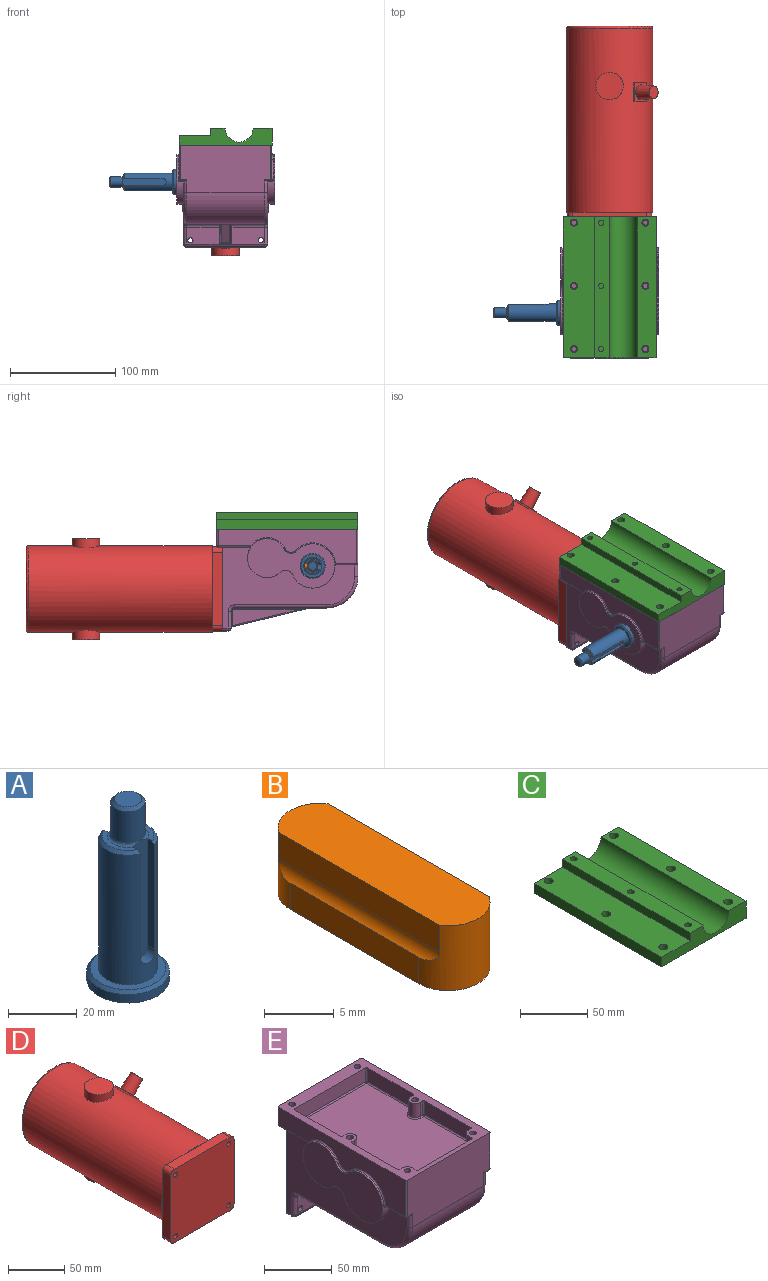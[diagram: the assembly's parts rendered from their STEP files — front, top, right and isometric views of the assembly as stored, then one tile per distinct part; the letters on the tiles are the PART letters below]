
ASSEMBLY  parts=5 mates=3
PART A: 21 faces, bbox 24x24x64 mm
  f0: plane 13.75x4.5mm, normal (0,0,1), area 22.7mm2, adj f4,f14,f17,f20
  f1: plane 13.75x4.5mm, normal (0,0,1), area 22.7mm2, adj f3,f12,f16,f20
  f2: cylinder r=8.5mm len=46mm, axis (0,0,1), area 1974.2mm2, adj f3,f4,f7,f12,f13,f14,f16,f17
  f3: cone r=7.5mm half-angle=45deg, axis (0,0,-1), area 26.8mm2, adj f1,f2,f12,f16
  f4: cone r=7.5mm half-angle=45deg, axis (0,0,-1), area 26.8mm2, adj f0,f2,f14,f17
  f5: plane 24x24mm, normal (0,0,-1), area 452.4mm2, adj f6
  f6: cylinder r=12mm len=24mm, axis (0,0,1), area 226.2mm2, adj f5,f10
  f7: plane 22x22mm, normal (0,0,1), area 153.2mm2, adj f2,f10
  f8: cylinder r=4.98mm len=11mm, axis (0,0,1), area 344.2mm2, adj f11,f20
  f9: plane 7.96x7.96mm, normal (0,0,1), area 49.8mm2, adj f11
  f10: cone r=11mm half-angle=45deg, axis (0,0,-1), area 102.2mm2, adj f6,f7
  f11: cone r=3.98mm half-angle=45deg, axis (0,0,-1), area 39.8mm2, adj f8,f9
  f12: plane 38.04x2.98mm, normal (1,0,0), area 111.7mm2, adj f1,f2,f3,f13,f15,f20
  f13: cylinder r=3mm len=6mm, axis (0,-1,0), area 30.4mm2, adj f2,f12,f14,f15
  f14: plane 38.04x2.98mm, normal (-1,0,0), area 111.7mm2, adj f0,f2,f4,f13,f15,f20
  f15: plane 41.8x6mm, normal (0,1,0), area 244.4mm2, adj f12,f13,f14,f20
  f16: plane 38.04x2.98mm, normal (1,0,0), area 111.7mm2, adj f1,f2,f3,f18,f19,f20
  f17: plane 38.04x2.98mm, normal (-1,0,0), area 111.7mm2, adj f0,f2,f4,f18,f19,f20
  f18: cylinder r=3mm len=6mm, axis (0,1,0), area 30.4mm2, adj f2,f16,f17,f19
  f19: plane 41.8x6mm, normal (0,-1,0), area 244.4mm2, adj f16,f17,f18,f20
  f20: torus R=5.98mm, axis (0,0,1), area 42.4mm2, adj f0,f1,f8,f12,f14,f15,f16,f17
PART B: 10 faces, bbox 6x19.1x5.7 mm
  f0: cylinder r=3mm len=6mm, axis (0,0,-1), area 42.5mm2, adj f1,f3,f4,f5,f6,f7,f8,f9
  f1: plane 13.05x2.32mm, normal (1,0,0), area 30.2mm2, adj f0,f2,f5,f8
  f2: cylinder r=3mm len=6mm, axis (0,0,-1), area 42.5mm2, adj f1,f3,f4,f5,f6,f7,f8,f9
  f3: plane 19.05x5mm, normal (0,0,1), area 91.3mm2, adj f0,f2,f7,f9
  f4: plane 13.05x2.32mm, normal (-1,0,0), area 30.2mm2, adj f0,f2,f5,f6
  f5: plane 19.05x6mm, normal (0,0,-1), area 106.6mm2, adj f0,f1,f2,f4
  f6: cylinder r=1.27mm len=16.37mm, axis (0,-1,0), area 18.3mm2, adj f0,f2,f4,f7
  f7: plane 16.37x2.37mm, normal (-1,0,0), area 38.9mm2, adj f0,f2,f3,f6
  f8: cylinder r=1.27mm len=16.37mm, axis (0,-1,0), area 18.3mm2, adj f0,f1,f2,f9
  f9: plane 16.37x2.37mm, normal (1,0,0), area 38.9mm2, adj f0,f2,f3,f8
PART C: 22 faces, bbox 88.3x134x15.9 mm
  f0: plane 134x15.88mm, normal (1,0,0), area 2127.2mm2, adj f1,f7,f8,f9
  f1: plane 134x88.25mm, normal (0,0,-1), area 11614mm2, adj f0,f2,f8,f9,f16,f17,f18,f19
  f2: plane 134x8.8mm, normal (-1,0,0), area 1179.2mm2, adj f1,f3,f8,f9
  f3: plane 134x29.8mm, normal (0,0,1), area 3887.4mm2, adj f2,f4,f8,f9,f19,f20,f21
  f4: plane 134x7.08mm, normal (-1,0,0), area 948mm2, adj f3,f5,f8,f9
  f5: plane 134x13.75mm, normal (0,0,1), area 1783.6mm2, adj f4,f6,f8,f9,f10,f12,f14
  f6: cylinder r=13.36mm len=134mm, axis (0,1,0), area 5520.3mm2, adj f5,f7,f8,f9
  f7: plane 134x18mm, normal (0,0,1), area 2306.2mm2, adj f0,f6,f8,f9,f16,f17,f18
  f8: plane 88.25x15.88mm, normal (0,-1,0), area 920.1mm2, adj f0,f1,f2,f3,f4,f5,f6,f7
  f9: plane 88.25x15.88mm, normal (0,1,0), area 920.1mm2, adj f0,f1,f2,f3,f4,f5,f6,f7
  f10: cylinder r=2.5mm len=7.08mm, axis (0,0,-1), area 111.1mm2, adj f5,f11
  f11: plane 5x5mm, normal (0,0,1), area 19.6mm2, adj f10
  f12: cylinder r=2.5mm len=7.08mm, axis (0,0,-1), area 111.1mm2, adj f5,f13
  f13: plane 5x5mm, normal (0,0,1), area 19.6mm2, adj f12
  f14: cylinder r=2.5mm len=7.08mm, axis (0,0,-1), area 111.1mm2, adj f5,f15
  f15: plane 5x5mm, normal (0,0,1), area 19.6mm2, adj f14
  f16: cylinder r=3.35mm len=15.88mm, axis (0,0,1), area 334.1mm2, adj f1,f7
  f17: cylinder r=3.35mm len=15.88mm, axis (0,0,1), area 334.1mm2, adj f1,f7
  f18: cylinder r=3.35mm len=15.88mm, axis (0,0,1), area 334.1mm2, adj f1,f7
  f19: cylinder r=3.35mm len=8.8mm, axis (0,0,1), area 185.2mm2, adj f1,f3
  f20: cylinder r=3.35mm len=8.8mm, axis (0,0,1), area 185.2mm2, adj f1,f3
  f21: cylinder r=3.35mm len=8.8mm, axis (0,0,1), area 185.2mm2, adj f1,f3
PART D: 35 faces, bbox 90.4x187x96 mm
  f0: cylinder r=41mm len=175mm, axis (0,-1,0), area 43714.5mm2, adj f1,f2,f3,f12,f14,f15,f16,f18
  f1: plane 31x31mm, normal (0,1,0), area 266.8mm2, adj f0,f4,f7,f11,f33
  f2: plane 31x31mm, normal (0,1,0), area 266.8mm2, adj f0,f6,f8,f11,f32
  f3: plane 31x31mm, normal (0,1,0), area 266.8mm2, adj f0,f5,f6,f9,f31
  f4: plane 70x10mm, normal (1,0,0), area 700mm2, adj f1,f12,f13,f16,f30,f33
  f5: plane 70x10mm, normal (0,0,-1), area 700mm2, adj f3,f12,f13,f18,f30,f31
  f6: plane 70x10mm, normal (-1,0,0), area 700mm2, adj f2,f3,f13,f15,f31,f32
  f7: cylinder r=2.5mm len=10mm, axis (0,-1,0), area 157.1mm2, adj f1,f13
  f8: cylinder r=2.5mm len=10mm, axis (0,-1,0), area 157.1mm2, adj f2,f13
  f9: cylinder r=2.5mm len=10mm, axis (0,-1,0), area 157.1mm2, adj f3,f13
  f10: cylinder r=2.5mm len=10mm, axis (0,-1,0), area 157.1mm2, adj f12,f13
  f11: plane 70x10mm, normal (0,0,1), area 700mm2, adj f1,f2,f13,f14,f32,f33
  f12: plane 31x31mm, normal (0,1,0), area 266.8mm2, adj f0,f4,f5,f10,f30
  f13: plane 80x80mm, normal (0,-1,0), area 6300mm2, adj f4,f5,f6,f7,f8,f9,f10,f11
  f14: plane 18x1mm, normal (0,-1,0), area 12mm2, adj f0,f11
  f15: plane 18x1mm, normal (0,-1,0), area 12mm2, adj f0,f6
  f16: plane 18x1mm, normal (0,-1,0), area 12mm2, adj f0,f4
  f17: plane 78x78mm, normal (0,1,0), area 4778.4mm2, adj f34
  f18: plane 18x1mm, normal (0,-1,0), area 12mm2, adj f0,f5
  f19: plane 26x26mm, normal (0,0,1), area 530.9mm2, adj f20
  f20: cylinder r=13mm len=26mm, axis (0,0,-1), area 657.6mm2, adj f0,f19
  f21: cylinder r=13mm len=26mm, axis (0,0,-1), area 657.6mm2, adj f0,f22
  f22: plane 26x26mm, normal (0,0,-1), area 530.9mm2, adj f21
  f23: plane 18x1.26mm, normal (-0.71,0,0.71), area 32.2mm2, adj f0,f25,f26,f27
  f24: plane 18x1.26mm, normal (0.71,0,-0.71), area 32.2mm2, adj f0,f25,f26,f27
  f25: plane 12.58x12.58mm, normal (0,1,0), area 20.2mm2, adj f0,f23,f24,f27
  f26: plane 12.58x12.58mm, normal (0,-1,0), area 20.2mm2, adj f0,f23,f24,f27
  f27: plane 18x11.31mm, normal (0.71,0,0.71), area 134.1mm2, adj f23,f24,f25,f26,f28
  f28: cone r=7mm half-angle=3deg, axis (-0.71,0,-0.71), area 701.1mm2, adj f27,f29
  f29: plane 12.22x8.64mm, normal (0.71,0,0.71), area 117.2mm2, adj f28
  f30: cylinder r=5mm len=10mm, axis (0,-1,0), area 78.5mm2, adj f4,f5,f12,f13
  f31: cylinder r=5mm len=10mm, axis (0,1,0), area 78.5mm2, adj f3,f5,f6,f13
  f32: cylinder r=5mm len=10mm, axis (0,-1,0), area 78.5mm2, adj f2,f6,f11,f13
  f33: cylinder r=5mm len=10mm, axis (0,1,0), area 78.5mm2, adj f1,f4,f11,f13
  f34: torus R=39mm, axis (0,1,0), area 795mm2, adj f0,f17
PART E: 163 faces, bbox 93x136.5x97 mm
  f0: cylinder r=3mm len=31mm, axis (1,0,0), area 146.1mm2, adj f3,f10,f45,f150
  f1: plane 134x88mm, normal (0,0,1), area 2921.3mm2, adj f2,f24,f25,f26,f48,f57,f64,f69
  f2: plane 86x45mm, normal (0,-1,0), area 3726mm2, adj f1,f31,f32,f34,f48,f49,f56,f57
  f3: plane 87.5x74mm, normal (0,0,-1), area 5616.9mm2, adj f0,f31,f35,f41,f42,f149,f151,f154
  f4: plane 80x80mm, normal (0,1,0), area 6317.6mm2, adj f5,f6,f7,f8,f9,f11,f13,f23
  f5: plane 125.5x77mm, normal (1,0,0), area 4068.3mm2, adj f4,f19,f20,f21,f22,f23,f32,f33
  f6: plane 125.5x77mm, normal (-1,0,0), area 4068.3mm2, adj f4,f15,f16,f17,f18,f23,f34,f38
  f7: plane 74x5mm, normal (0,0,-1), area 370mm2, adj f4,f37,f43,f44
  f8: cylinder r=2.5mm len=8mm, axis (0,1,0), area 125.7mm2, adj f4,f10
  f9: cylinder r=2.5mm len=8mm, axis (0,1,0), area 125.7mm2, adj f4,f10
  f10: plane 74x16mm, normal (0,-1,0), area 957mm2, adj f0,f8,f9,f36,f42,f43,f47,f152
  f11: cylinder r=2.5mm len=6mm, axis (0,1,0), area 94.2mm2, adj f4,f12
  f12: plane 5x5mm, normal (0,1,0), area 19.6mm2, adj f11
  f13: cylinder r=2.5mm len=6mm, axis (0,1,0), area 94.2mm2, adj f4,f14
  f14: plane 5x5mm, normal (0,1,0), area 19.6mm2, adj f13
  f15: plane 20x3.76mm, normal (0,0,-1), area 60.5mm2, adj f6,f34,f49,f51,f52
  f16: cylinder r=21mm len=42mm, axis (-1,0,0), area 449.8mm2, adj f6,f17,f27,f28,f52,f53,f54
  f17: cylinder r=7.11mm len=11.42mm, axis (-1,0,0), area 88.9mm2, adj f6,f16,f18,f27
  f18: cylinder r=18.5mm len=37mm, axis (-1,0,0), area 402.3mm2, adj f6,f17,f27,f28,f58,f59,f61
  f19: plane 20x3.76mm, normal (0,0,-1), area 60.5mm2, adj f5,f32,f56,f62,f63
  f20: cylinder r=21mm len=42mm, axis (-1,0,0), area 449.8mm2, adj f5,f21,f29,f30,f62,f66,f68
  f21: cylinder r=7.11mm len=11.42mm, axis (-1,0,0), area 88.9mm2, adj f5,f20,f22,f30
  f22: cylinder r=18.5mm len=37mm, axis (-1,0,0), area 402.3mm2, adj f5,f21,f29,f30,f73,f75,f76
  f23: plane 86x29.51mm, normal (0,0,-1), area 537.1mm2, adj f4,f5,f6,f59,f65,f70,f74,f76
  f24: plane 86x16mm, normal (0,1,0), area 1376mm2, adj f1,f64,f69,f70
  f25: plane 132x33mm, normal (1,0,0), area 2354mm2, adj f1,f57,f63,f68,f69,f71,f73,f74
  f26: plane 132x33mm, normal (-1,0,0), area 2354mm2, adj f1,f48,f51,f54,f55,f58,f64,f65
  f27: plane 82.96x47mm, normal (-1,0,0), area 2565.2mm2, adj f16,f17,f18,f28
  f28: cylinder r=7.11mm len=11.55mm, axis (-1,0,0), area 20.5mm2, adj f16,f18,f27,f55
  f29: cylinder r=7.11mm len=11.55mm, axis (-1,0,0), area 20.5mm2, adj f20,f22,f30,f71
  f30: plane 82.96x47mm, normal (1,0,0), area 2565.2mm2, adj f20,f21,f22,f29
  f31: cylinder r=30mm len=74mm, axis (1,0,0), area 3487.2mm2, adj f2,f3,f33,f38
  f32: cylinder r=3mm len=12mm, axis (0,0,1), area 53.1mm2, adj f2,f5,f19,f33,f56
  f33: torus R=27mm, axis (1,0,0), area 214mm2, adj f5,f31,f32,f35
  f34: cylinder r=3mm len=12mm, axis (0,0,-1), area 53.1mm2, adj f2,f6,f15,f38,f49
  f35: cylinder r=3mm len=87.5mm, axis (0,-1,0), area 412.3mm2, adj f3,f5,f33,f39
  f36: cylinder r=3mm len=16mm, axis (0,0,-1), area 75.4mm2, adj f5,f10,f39,f40
  f37: cylinder r=3mm len=5mm, axis (0,-1,0), area 23.6mm2, adj f4,f5,f7,f40
  f38: torus R=27mm, axis (1,0,0), area 214mm2, adj f6,f31,f34,f41
  f39: torus R=6mm, axis (1,0,0), area 30.3mm2, adj f5,f35,f36,f42
  f40: sphere r=3mm, area 14.1mm2, adj f36,f37,f43
  f41: cylinder r=3mm len=87.5mm, axis (0,1,0), area 412.3mm2, adj f3,f6,f38,f45
  f42: cylinder r=3mm len=31mm, axis (1,0,0), area 146.1mm2, adj f3,f10,f39,f160
  f43: cylinder r=3mm len=74mm, axis (-1,0,0), area 348.7mm2, adj f7,f10,f40,f46
  f44: cylinder r=3mm len=5mm, axis (0,1,0), area 23.6mm2, adj f4,f6,f7,f46
  f45: torus R=6mm, axis (1,0,0), area 30.3mm2, adj f0,f6,f41,f47
  f46: sphere r=3mm, area 14.1mm2, adj f43,f44,f47
  f47: cylinder r=3mm len=16mm, axis (0,0,1), area 75.4mm2, adj f6,f10,f45,f46
  f48: cylinder r=1mm len=33mm, axis (0,0,-1), area 51.8mm2, adj f1,f2,f26,f50
  f49: cylinder r=1mm len=6mm, axis (-1,0,0), area 7.7mm2, adj f2,f15,f34,f50
  f50: sphere r=1mm, area 1.6mm2, adj f48,f49,f51
  f51: cylinder r=1mm len=20.09mm, axis (0,1,0), area 31.5mm2, adj f15,f26,f50,f53
  f52: cylinder r=1mm len=3mm, axis (-1,0,0), area 4.7mm2, adj f6,f15,f16,f53
  f53: bspline ~2.45x2.23mm, area 3.3mm2, adj f16,f51,f52,f54
  f54: torus R=22mm, axis (1,0,0), area 77.3mm2, adj f16,f26,f53,f55
  f55: torus R=6.11mm, axis (1,0,0), area 20.4mm2, adj f26,f28,f54,f58
  f56: cylinder r=1mm len=6mm, axis (-1,0,0), area 7.7mm2, adj f2,f19,f32,f60
  f57: cylinder r=1mm len=33mm, axis (0,0,1), area 51.8mm2, adj f1,f2,f25,f60
  f58: torus R=19.5mm, axis (1,0,0), area 60.5mm2, adj f18,f26,f55,f61
  f59: cylinder r=1mm len=3mm, axis (-1,0,0), area 6.2mm2, adj f6,f18,f23,f61
  f60: sphere r=1mm, area 1.6mm2, adj f56,f57,f63
  f61: bspline ~2.77x2.49mm, area 4.3mm2, adj f18,f58,f59,f65
  f62: cylinder r=1mm len=3mm, axis (-1,0,0), area 4.7mm2, adj f5,f19,f20,f66
  f63: cylinder r=1mm len=20.09mm, axis (0,-1,0), area 31.5mm2, adj f19,f25,f60,f66
  f64: cylinder r=1mm len=16mm, axis (0,0,1), area 25.1mm2, adj f1,f24,f26,f67
  f65: cylinder r=1mm len=30.79mm, axis (0,1,0), area 47.1mm2, adj f23,f26,f61,f67
  f66: bspline ~2.34x2.34mm, area 3.3mm2, adj f20,f62,f63,f68
  f67: sphere r=1mm, area 1.6mm2, adj f64,f65,f70
  f68: torus R=22mm, axis (1,0,0), area 77.3mm2, adj f20,f25,f66,f71
  f69: cylinder r=1mm len=16mm, axis (0,0,-1), area 25.1mm2, adj f1,f24,f25,f72
  f70: cylinder r=1mm len=86mm, axis (-1,0,0), area 135.1mm2, adj f23,f24,f67,f72
  f71: torus R=6.11mm, axis (1,0,0), area 20.4mm2, adj f25,f29,f68,f73
  f72: sphere r=1mm, area 1.6mm2, adj f69,f70,f74
  f73: torus R=19.5mm, axis (1,0,0), area 60.5mm2, adj f22,f25,f71,f75
  f74: cylinder r=1mm len=30.79mm, axis (0,-1,0), area 47.1mm2, adj f23,f25,f72,f75
  f75: bspline ~2.7x2.4mm, area 4.3mm2, adj f22,f73,f74,f76
  f76: cylinder r=1mm len=3mm, axis (-1,0,0), area 6.2mm2, adj f5,f22,f23,f75
  f77: plane 56x12.5mm, normal (0,1,0), area 700mm2, adj f1,f139,f143,f145
  f78: plane 12.5x4mm, normal (-1,0,0), area 50mm2, adj f1,f79,f138,f139
  f79: cylinder r=5mm len=12.5mm, axis (0,0,1), area 98.2mm2, adj f1,f78,f80,f136
  f80: plane 12.5x3mm, normal (0,1,0), area 37.5mm2, adj f1,f79,f129,f134
  f81: plane 48x12.5mm, normal (-1,0,0), area 600mm2, adj f1,f123,f128,f129
  f82: plane 12.5x3mm, normal (0,-1,0), area 37.5mm2, adj f1,f83,f122,f123
  f83: cylinder r=5mm len=12.5mm, axis (0,0,1), area 196.3mm2, adj f1,f82,f84,f120
  f84: plane 12.5x3mm, normal (0,1,0), area 37.5mm2, adj f1,f83,f113,f118
  f85: plane 47.5x12.5mm, normal (-1,0,0), area 593.8mm2, adj f1,f108,f112,f113
  f86: plane 74x12.5mm, normal (0,-1,0), area 925mm2, adj f1,f108,f110,f111
  f87: plane 47.5x12.5mm, normal (1,0,0), area 593.8mm2, adj f1,f110,f116,f117
  f88: plane 12.5x3mm, normal (0,1,0), area 37.5mm2, adj f1,f89,f116,f121
  f89: cylinder r=5mm len=12.5mm, axis (0,0,1), area 196.3mm2, adj f1,f88,f90,f124
  f90: plane 12.5x3mm, normal (0,-1,0), area 37.5mm2, adj f1,f89,f126,f127
  f91: plane 48x12.5mm, normal (1,0,0), area 600mm2, adj f1,f126,f132,f133
  f92: plane 12.5x3mm, normal (0,1,0), area 37.5mm2, adj f1,f93,f132,f137
  f93: cylinder r=5mm len=12.5mm, axis (0,0,1), area 98.2mm2, adj f1,f92,f94,f140
  f94: plane 12.5x4mm, normal (1,0,0), area 50mm2, adj f1,f93,f142,f145
  f95: plane 117.5x74mm, normal (0,0,1), area 8345.4mm2, adj f111,f112,f117,f118,f120,f121,f122,f124
  f96: cylinder r=2.5mm len=13.5mm, axis (0,0,1), area 212.1mm2, adj f1,f97
  f97: plane 5x5mm, normal (0,0,1), area 19.6mm2, adj f96
  f98: cylinder r=2.5mm len=13.5mm, axis (0,0,1), area 212.1mm2, adj f1,f99
  f99: plane 5x5mm, normal (0,0,1), area 19.6mm2, adj f98
  f100: cylinder r=2.5mm len=13.5mm, axis (0,0,1), area 212.1mm2, adj f1,f101
  f101: plane 5x5mm, normal (0,0,1), area 19.6mm2, adj f100
  f102: cylinder r=2.5mm len=13.5mm, axis (0,0,1), area 212.1mm2, adj f1,f103
  f103: plane 5x5mm, normal (0,0,1), area 19.6mm2, adj f102
  f104: cylinder r=2.5mm len=13.5mm, axis (0,0,1), area 212.1mm2, adj f1,f105
  f105: plane 5x5mm, normal (0,0,1), area 19.6mm2, adj f104
  f106: cylinder r=2.5mm len=13.5mm, axis (0,0,1), area 212.1mm2, adj f1,f107
  f107: plane 5x5mm, normal (0,0,1), area 19.6mm2, adj f106
  f108: cylinder r=1mm len=12.5mm, axis (0,0,1), area 19.6mm2, adj f1,f85,f86,f109
  f109: sphere r=1mm, area 1.6mm2, adj f108,f111,f112
  f110: cylinder r=1mm len=12.5mm, axis (0,0,-1), area 19.6mm2, adj f1,f86,f87,f114
  f111: cylinder r=1mm len=74mm, axis (-1,0,0), area 116.2mm2, adj f86,f95,f109,f114
  f112: cylinder r=1mm len=47.5mm, axis (0,1,0), area 74.6mm2, adj f85,f95,f109,f115
  f113: cylinder r=1mm len=12.5mm, axis (0,0,1), area 19.6mm2, adj f1,f84,f85,f115
  f114: sphere r=1mm, area 1.6mm2, adj f110,f111,f117
  f115: sphere r=1mm, area 1.6mm2, adj f112,f113,f118
  f116: cylinder r=1mm len=12.5mm, axis (0,0,1), area 19.6mm2, adj f1,f87,f88,f119
  f117: cylinder r=1mm len=47.5mm, axis (0,-1,0), area 74.6mm2, adj f87,f95,f114,f119
  f118: cylinder r=1mm len=3mm, axis (1,0,0), area 4.7mm2, adj f84,f95,f115,f120
  f119: sphere r=1mm, area 1.6mm2, adj f116,f117,f121
  f120: torus R=6mm, axis (0,0,1), area 26.5mm2, adj f83,f95,f118,f122
  f121: cylinder r=1mm len=3mm, axis (1,0,0), area 4.7mm2, adj f88,f95,f119,f124
  f122: cylinder r=1mm len=3mm, axis (-1,0,0), area 4.7mm2, adj f82,f95,f120,f125
  f123: cylinder r=1mm len=12.5mm, axis (0,0,-1), area 19.6mm2, adj f1,f81,f82,f125
  f124: torus R=6mm, axis (0,0,1), area 26.5mm2, adj f89,f95,f121,f127
  f125: sphere r=1mm, area 1.6mm2, adj f122,f123,f128
  f126: cylinder r=1mm len=12.5mm, axis (0,0,-1), area 19.6mm2, adj f1,f90,f91,f130
  f127: cylinder r=1mm len=3mm, axis (-1,0,0), area 4.7mm2, adj f90,f95,f124,f130
  f128: cylinder r=1mm len=48mm, axis (0,1,0), area 75.4mm2, adj f81,f95,f125,f131
  f129: cylinder r=1mm len=12.5mm, axis (0,0,1), area 19.6mm2, adj f1,f80,f81,f131
  f130: sphere r=1mm, area 1.6mm2, adj f126,f127,f133
  f131: sphere r=1mm, area 1.6mm2, adj f128,f129,f134
  f132: cylinder r=1mm len=12.5mm, axis (0,0,1), area 19.6mm2, adj f1,f91,f92,f135
  f133: cylinder r=1mm len=48mm, axis (0,-1,0), area 75.4mm2, adj f91,f95,f130,f135
  f134: cylinder r=1mm len=3mm, axis (1,0,0), area 4.7mm2, adj f80,f95,f131,f136
  f135: sphere r=1mm, area 1.6mm2, adj f132,f133,f137
  f136: torus R=6mm, axis (0,0,1), area 13.2mm2, adj f79,f95,f134,f138
  f137: cylinder r=1mm len=3mm, axis (1,0,0), area 4.7mm2, adj f92,f95,f135,f140
  f138: cylinder r=1mm len=4mm, axis (0,1,0), area 6.3mm2, adj f78,f95,f136,f141
  f139: cylinder r=1mm len=12.5mm, axis (0,0,-1), area 19.6mm2, adj f1,f77,f78,f141
  f140: torus R=6mm, axis (0,0,1), area 13.2mm2, adj f93,f95,f137,f142
  f141: sphere r=1mm, area 1.6mm2, adj f138,f139,f143
  f142: cylinder r=1mm len=4mm, axis (0,-1,0), area 6.3mm2, adj f94,f95,f140,f144
  f143: cylinder r=1mm len=56mm, axis (1,0,0), area 88mm2, adj f77,f95,f141,f144
  f144: sphere r=1mm, area 1.6mm2, adj f142,f143,f145
  f145: cylinder r=1mm len=12.5mm, axis (0,0,1), area 19.6mm2, adj f1,f77,f94,f144
  f146: plane 65.55x15.73mm, normal (1,0,0), area 514.7mm2, adj f157,f159,f160,f162
  f147: plane 65.55x15.73mm, normal (-1,0,0), area 514.7mm2, adj f149,f150,f152,f153
  f148: plane 74.12x17.79mm, normal (0,-0.23,-0.97), area 609.8mm2, adj f153,f154,f158,f159
  f149: cylinder r=1mm len=63.55mm, axis (0,1,0), area 99.8mm2, adj f3,f147,f150,f151
  f150: torus R=2mm, axis (1,0,0), area 6.5mm2, adj f0,f147,f149,f152
  f151: bspline ~8.57x2mm, area 8.8mm2, adj f3,f149,f153,f154
  f152: cylinder r=1mm len=13.73mm, axis (0,0,-1), area 21.6mm2, adj f10,f147,f150,f155
  f153: cylinder r=1mm len=74.35mm, axis (0,0.97,-0.23), area 114.6mm2, adj f147,f148,f151,f155
  f154: cylinder r=1mm len=8mm, axis (1,0,0), area 1.9mm2, adj f3,f148,f151,f156
  f155: bspline ~2.14x2.06mm, area 3.2mm2, adj f10,f152,f153,f158
  f156: bspline ~8.57x2mm, area 8.8mm2, adj f3,f154,f157,f159
  f157: cylinder r=1mm len=63.55mm, axis (0,-1,0), area 99.8mm2, adj f3,f146,f156,f160
  f158: cylinder r=1mm len=8mm, axis (1,0,0), area 10.7mm2, adj f10,f148,f155,f161
  f159: cylinder r=1mm len=74.35mm, axis (0,-0.97,0.23), area 114.6mm2, adj f146,f148,f156,f161
  f160: torus R=2mm, axis (1,0,0), area 6.5mm2, adj f42,f146,f157,f162
  f161: bspline ~2.41x2.35mm, area 3.2mm2, adj f10,f158,f159,f162
  f162: cylinder r=1mm len=13.73mm, axis (0,0,1), area 21.6mm2, adj f10,f146,f160,f161
PLACE A rot(axis=(0,-1,0),90deg) t=(-46.5,-85.5,22)mm
PLACE B rot(axis=(-0.58,0.58,0.58),120deg) t=(-76.5,-80.5,22)mm
PLACE C at identity
PLACE D t=(0,0,0.02)mm
PLACE E at identity fixed
MATE fastened C.f16 <-> E.f79  axis (0,0,-1) through (34,-120,57)mm
MATE revolute A.f10 <-> E.f16  axis (1,0,0) through (-46.5,-85.5,22)mm
MATE fastened E.f4 <-> D.f0  axis (0,1,0) through (0,0,0.02)mm
